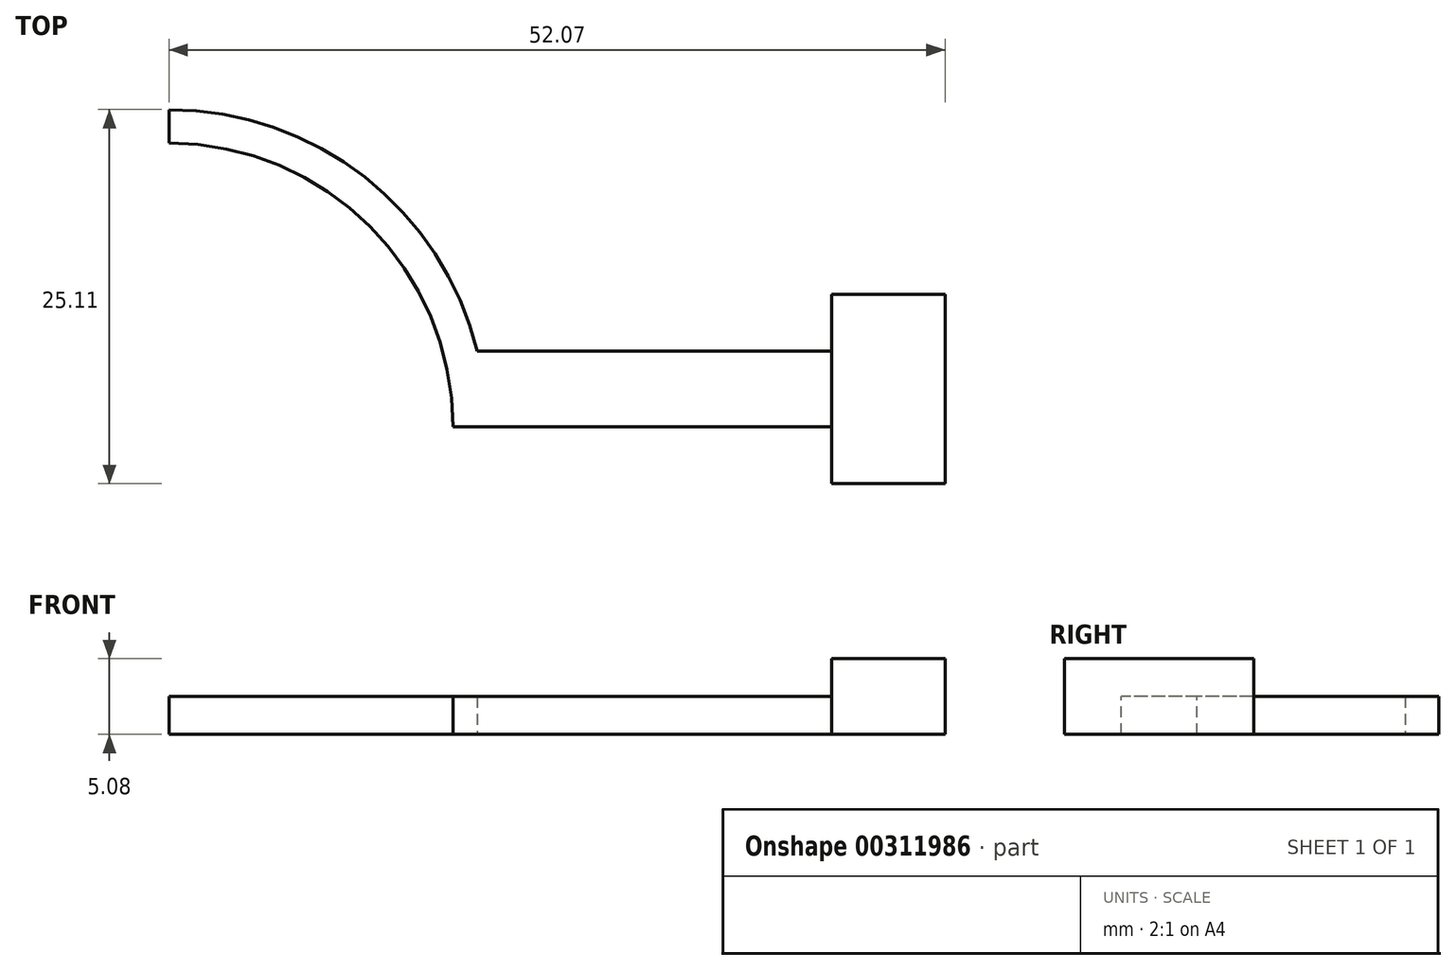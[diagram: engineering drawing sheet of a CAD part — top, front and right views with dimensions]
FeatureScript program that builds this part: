
annotation { "Feature Type Name" : "Feature", "Feature Type Description" : "" }
export const myFeature = defineFeature(function(context is Context, id is Id, definition is map)
    precondition{}
    {
        {
            var Q0;
            Q0=qCreatedBy(makeId("Top.planeOp"),FACE);
            var sketch = newSketch(context, id + "F0", { "sketchPlane" : qUnion([Q0])});
            skLineSegment(sketch, "E0.bottom", {"start": v(-69.75, 19.59) * mm, "end": v(-62.13, 19.59) * mm});
            skLineSegment(sketch, "E0.top", {"start": v(-69.75, 6.89) * mm, "end": v(-62.13, 6.89) * mm});
            skLineSegment(sketch, "E0.left", {"start": v(-69.75, 19.59) * mm, "end": v(-69.75, 6.89) * mm});
            skLineSegment(sketch, "E0.right", {"start": v(-62.13, 19.59) * mm, "end": v(-62.13, 6.89) * mm});
            skSolve(sketch);
        }
        {
            var Q0;
            Q0 = qSketchRegion(id + "F0", true);
            extrude(context, id + "F1", {"entities" : qUnion([Q0]), "depth" : 5.08 * mm});
        }
        {
            var Q0;
            Q0=makeQuery(id+"F1.opExtrude","SWEPT_FACE",FACE,{"disambiguationData":[OSD([sQuery(id+"F0.wireOp",EDGE,"E0.left")])]});
            var sketch = newSketch(context, id + "F2", { "sketchPlane" : qUnion([Q0])});
            skLineSegment(sketch, "E1.bottom", {"start": v(-15.78, 0) * mm, "end": v(-10.7, 0) * mm});
            skLineSegment(sketch, "E1.top", {"start": v(-15.78, 2.54) * mm, "end": v(-10.7, 2.54) * mm});
            skLineSegment(sketch, "E1.left", {"start": v(-15.78, 0) * mm, "end": v(-15.78, 2.54) * mm});
            skLineSegment(sketch, "E1.right", {"start": v(-10.7, 0) * mm, "end": v(-10.7, 2.54) * mm});
            skPoint(sketch, "E1.middle", {"position": v(-13.24, 1.27) * mm});
            skPoint(sketch, "E1.middle.positionSnap0", {"position": v(-13.24, 0) * mm});
            skPoint(sketch, "E1.centerSnap0", {"position": v(-13.24, 0) * mm});
            skSolve(sketch);
        }
        {
            var Q0;
            Q0 = qSketchRegion(id + "F2", true);
            extrude(context, id + "F3", {"entities" : qUnion([Q0]), "operationType" : NewBodyOperationType.ADD, "depth" : 25.4 * mm});
        }
        {
            var Q0;
            Q0=makeQuery(id+"F3.boolean.opBoolean","MERGE",FACE,{"derivedFrom":[makeQuery(id+"F1.opExtrude","CAP_FACE",FACE,{"disambiguationData":[OSD([sQuery(id+"F0.wireOp",EDGE,"E0.bottom"),sQuery(id+"F0.wireOp",EDGE,"E0.top"),sQuery(id+"F0.wireOp",EDGE,"E0.left"),sQuery(id+"F0.wireOp",EDGE,"E0.right")])],"isStart":true}),makeQuery(id+"F3.opExtrude","SWEPT_FACE",FACE,{"disambiguationData":[OSD([sQuery(id+"F2.wireOp",EDGE,"E1.bottom")])]})]});
            var sketch = newSketch(context, id + "F4", { "sketchPlane" : qUnion([Q0])});
            skLineSegment(sketch, "E2.0", {"start": v(-95.15, -15.78) * mm, "end": v(-95.15, -10.7) * mm});
            skLineSegment(sketch, "E3.0", {"start": v(-95.15, -15.78) * mm, "end": v(-69.75, -15.78) * mm});
            skLineSegment(sketch, "E4.0", {"start": v(-95.15, -10.7) * mm, "end": v(-69.75, -10.7) * mm});
            skPoint(sketch, "E5", {"position": v(-95.15, -20.22) * mm});
            skArc(sketch, "E6", {"start": v(-114.2, -29.75) * mm, "mid": v(-100.73, -24.17) * mm, "end": v(-95.15, -10.7) * mm});
            skLineSegment(sketch, "E7", {"start": v(-114.2, -29.75) * mm, "end": v(-114.2, -32) * mm});
            skArc(sketch, "E8", {"start": v(-114.2, -32) * mm, "mid": v(-99.14, -25.76) * mm, "end": v(-92.9, -10.7) * mm});
            skSolve(sketch);
        }
        {
            var Q0;
            {var subQ1=sQuery(id+"F4.wireOp",EDGE,"E3.0");var subQ3=sQuery(id+"F4.wireOp",EDGE,"QPUtcI3v-KCDb-YNj0-nne0-aU2mi0U8ZqbS");var subQ4=makeQuery(id+"F4.imprint","INTERSECT",VERTEX,{"derivedFrom":[subQ1,subQ3]});Q0=makeQuery(id+"F4.imprint","IMPRINT",FACE,{"disambiguationData":[TD([[makeQuery(id+"F4.imprint","IMPRINT",EDGE,{"disambiguationData":[TD([[subQ4,1.0]])],"derivedFrom":subQ3}),1.0]])]});}
            var Q1;
            {var subQ0=sQuery(id+"F4.wireOp",EDGE,"QPUtcI3v-KCDb-YNj0-nne0-aU2mi0U8ZqbS");var subQ1=sQuery(id+"F4.wireOp",EDGE,"E4.0");var subQ2=makeQuery(id+"F4.imprint","INTERSECT",VERTEX,{"derivedFrom":[subQ1,subQ0]});Q1=makeQuery(id+"F4.imprint","IMPRINT",FACE,{"disambiguationData":[TD([[makeQuery(id+"F4.imprint","IMPRINT",EDGE,{"disambiguationData":[TD([[subQ2,1.0]])],"derivedFrom":subQ1}),1.0]])]});}
            var Q2;
            {var subQ0=sQuery(id+"F4.wireOp",EDGE,"QPUtcI3v-KCDb-YNj0-nne0-aU2mi0U8ZqbS");var subQ1=sQuery(id+"F4.wireOp",EDGE,"vHNi9isE-zza3-qEnU-IXTJ-K0Utpjj81WnW.top");var subQ2=makeQuery(id+"F4.imprint","INTERSECT",VERTEX,{"derivedFrom":[subQ1,subQ0]});Q2=makeQuery(id+"F4.imprint","IMPRINT",FACE,{"disambiguationData":[TD([[makeQuery(id+"F4.imprint","IMPRINT",EDGE,{"disambiguationData":[TD([[subQ2,-1.0]])],"derivedFrom":subQ1}),-1.0]])]});}
            var Q3;
            {var subQ1=sQuery(id+"F4.wireOp",EDGE,"vHNi9isE-zza3-qEnU-IXTJ-K0Utpjj81WnW.top");var subQ3=sQuery(id+"F4.wireOp",EDGE,"fhxZ7U2Q-wudT-hAMa-Dhjf-427Xy0ghVFy4");var subQ4=makeQuery(id+"F4.imprint","INTERSECT",VERTEX,{"derivedFrom":[subQ1,subQ3]});Q3=makeQuery(id+"F4.imprint","IMPRINT",FACE,{"disambiguationData":[TD([[makeQuery(id+"F4.imprint","IMPRINT",EDGE,{"disambiguationData":[TD([[subQ4,-1.0]])],"derivedFrom":subQ1}),-1.0]])]});}
            var Q4;
            {var subQ1=sQuery(id+"F4.wireOp",EDGE,"E4.0");var subQ3=sQuery(id+"F4.wireOp",EDGE,"fhxZ7U2Q-wudT-hAMa-Dhjf-427Xy0ghVFy4");var subQ4=makeQuery(id+"F4.imprint","INTERSECT",VERTEX,{"derivedFrom":[subQ1,subQ3]});Q4=makeQuery(id+"F4.imprint","IMPRINT",FACE,{"disambiguationData":[TD([[makeQuery(id+"F4.imprint","IMPRINT",EDGE,{"disambiguationData":[TD([[subQ4,-1.0]])],"derivedFrom":subQ3}),1.0]])]});}
            var Q5;
            {var subQ3=sQuery(id+"F4.wireOp",EDGE,"QPUtcI3v-KCDb-YNj0-nne0-aU2mi0U8ZqbS");var subQ5=sQuery(id+"F4.wireOp",EDGE,"E4.0");var subQ6=makeQuery(id+"F4.imprint","INTERSECT",VERTEX,{"derivedFrom":[subQ5,subQ3]});Q5=makeQuery(id+"F4.imprint","IMPRINT",FACE,{"disambiguationData":[TD([[makeQuery(id+"F4.imprint","IMPRINT",EDGE,{"disambiguationData":[TD([[subQ6,1.0]])],"derivedFrom":subQ5}),-1.0]])]});}
            var Q6;
            {var subQ1=sQuery(id+"F4.wireOp",EDGE,"E4.0");var subQ3=sQuery(id+"F4.wireOp",EDGE,"fhxZ7U2Q-wudT-hAMa-Dhjf-427Xy0ghVFy4");var subQ4=makeQuery(id+"F4.imprint","INTERSECT",VERTEX,{"derivedFrom":[subQ1,subQ3]});Q6=makeQuery(id+"F4.imprint","IMPRINT",FACE,{"disambiguationData":[TD([[makeQuery(id+"F4.imprint","IMPRINT",EDGE,{"disambiguationData":[TD([[subQ4,1.0]])],"derivedFrom":subQ3}),1.0]])]});}
            var Q7;
            {var subQ2=sQuery(id+"F4.wireOp",EDGE,"E2.0");Q7=makeQuery(id+"F4.imprint","IMPRINT",FACE,{"disambiguationData":[TD([[makeQuery(id+"F4.imprint","IMPRINT",EDGE,{"derivedFrom":subQ2}),1.0]])]});}
            extrude(context, id + "F5", {"entities" : qUnion([Q0, Q1, Q2, Q3, Q4, Q5, Q6, Q7]), "operationType" : NewBodyOperationType.ADD, "oppositeDirection" : true, "depth" : 2.54 * mm});
        }
    });
